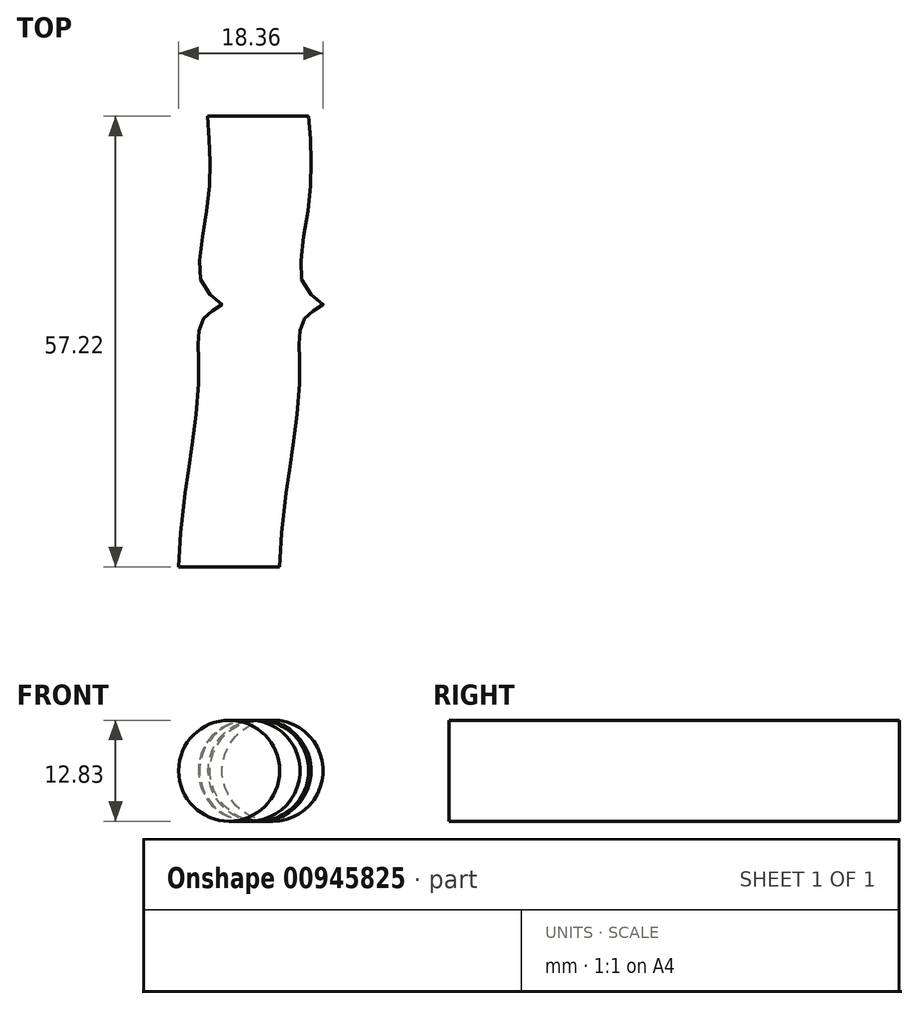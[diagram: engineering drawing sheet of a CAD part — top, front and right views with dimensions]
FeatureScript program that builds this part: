
annotation { "Feature Type Name" : "Feature", "Feature Type Description" : "" }
export const myFeature = defineFeature(function(context is Context, id is Id, definition is map)
    precondition{}
    {
        {
            var Q0;
            Q0=qCreatedBy(makeId("Front.planeOp"),FACE);
            var sketch = newSketch(context, id + "F0", { "sketchPlane" : qUnion([Q0])});
            skCircle(sketch, "E0", {"center": v(-110.2, 54.22) * mm, "radius": 6.42 * mm});
            skSolve(sketch);
        }
        {
            var Q0;
            Q0=qCreatedBy(makeId("Top.planeOp"),FACE);
            var sketch = newSketch(context, id + "F1", { "sketchPlane" : qUnion([Q0])});
            skFitSpline(sketch, "E1", {"points": [v(-164.61, 67.4) * mm, v(-164.61, 56.15) * mm, v(-164.98, 45.44) * mm, v(-162.77, 43.6) * mm, v(-164.98, 41.93) * mm, v(-165.72, 34.74) * mm, v(-167.56, 18.86) * mm, v(-168.3, 10.19) * mm], "startDerivative": vector(4.7, -62.4) * mm, "endDerivative": vector(-2.8, -51.84) * mm});
            skSolve(sketch);
        }
        {
            var Q0;
            Q0=makeQuery(id+"F0.imprint","IMPRINT",FACE,{"disambiguationData":[TD([[makeQuery(id+"F0.imprint","IMPRINT",EDGE,{"derivedFrom":sQuery(id+"F0.wireOp",EDGE,"E0")}),1.0]])]});
            var Q1;
            Q1=sQuery(id+"F1.wireOp",EDGE,"E1");
            sweep(context, id + "F2", {"profiles" : qUnion([Q0]), "path" : qUnion([Q1]), "keepProfileOrientation" : true});
        }
    });
